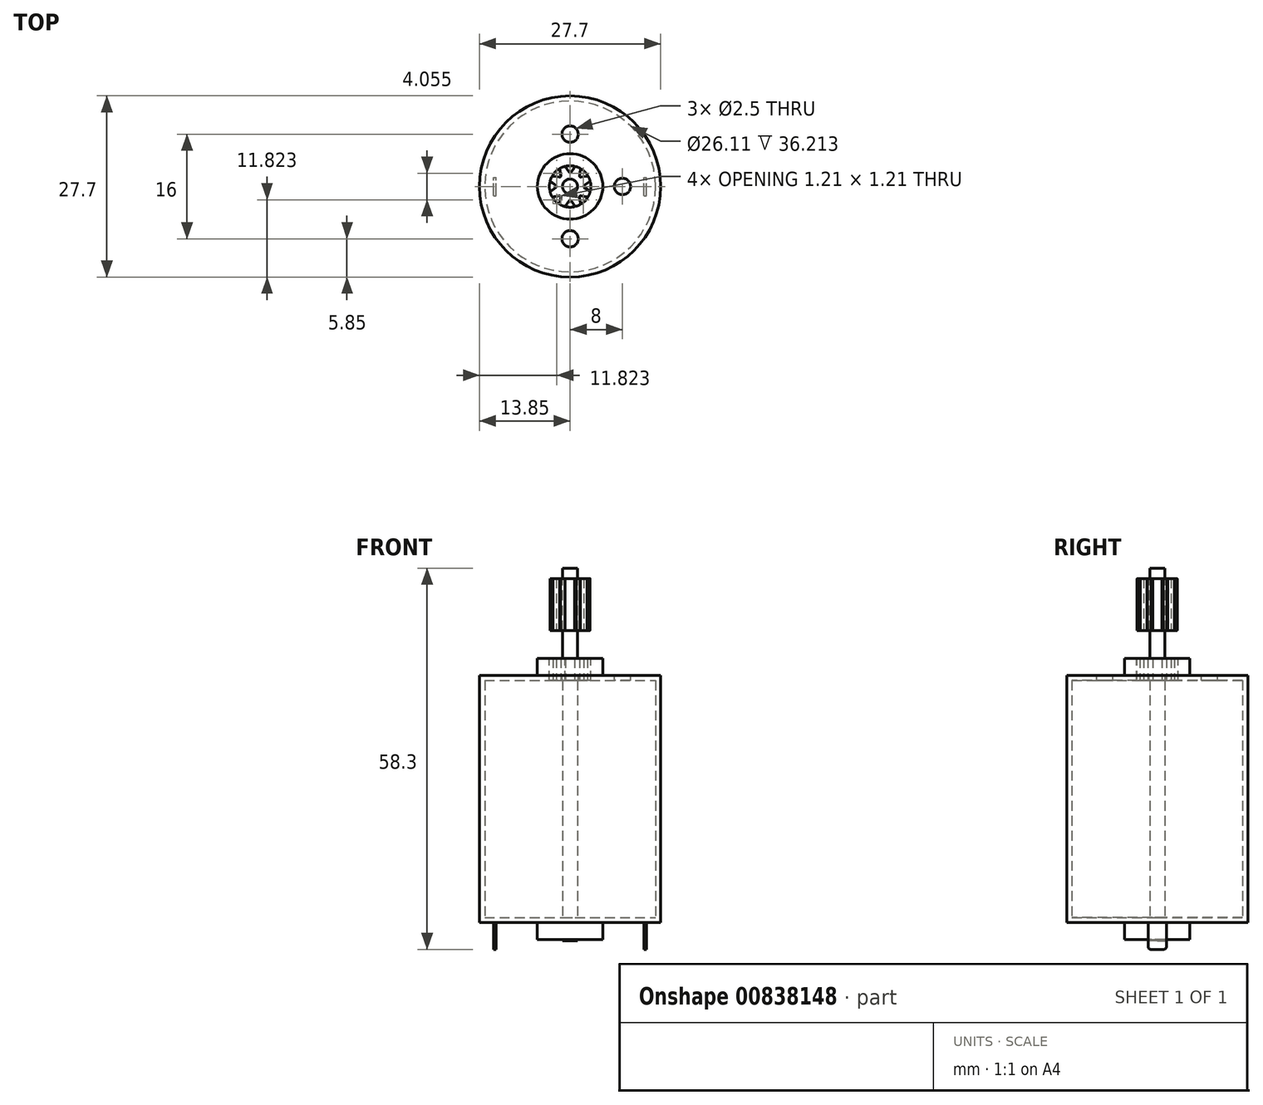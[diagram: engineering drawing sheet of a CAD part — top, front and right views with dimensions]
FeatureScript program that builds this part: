
annotation { "Feature Type Name" : "Feature", "Feature Type Description" : "" }
export const myFeature = defineFeature(function(context is Context, id is Id, definition is map)
    precondition{}
    {
        {
            var Q0;
            Q0=qCreatedBy(makeId("Top.planeOp"),FACE);
            var sketch = newSketch(context, id + "F0", { "sketchPlane" : qUnion([Q0])});
            skCircle(sketch, "E0", {"center": v(0, 0) * mm, "radius": 13.85 * mm});
            skSolve(sketch);
        }
        {
            var Q0;
            Q0=makeQuery(id+"F0.imprint","IMPRINT",FACE,{"disambiguationData":[TD([[makeQuery(id+"F0.imprint","IMPRINT",EDGE,{"derivedFrom":sQuery(id+"F0.wireOp",EDGE,"E0")}),1.0]])]});
            extrude(context, id + "F1", {"entities" : qUnion([Q0]), "depth" : 37.8 * mm, "offsetDistance" : 25.4 * mm});
        }
        {
            var Q0;
            Q0=makeQuery(id+"F1.opExtrude","CAP_FACE",FACE,{"disambiguationData":[OSD([sQuery(id+"F0.wireOp",EDGE,"E0")])],"isStart":false});
            var sketch = newSketch(context, id + "F2", { "sketchPlane" : qUnion([Q0])});
            skCircle(sketch, "E1", {"center": v(0, 0) * mm, "radius": 5 * mm});
            skSolve(sketch);
        }
        {
            var Q0;
            Q0=makeQuery(id+"F2.imprint","IMPRINT",FACE,{"disambiguationData":[TD([[makeQuery(id+"F2.imprint","IMPRINT",EDGE,{"derivedFrom":sQuery(id+"F2.wireOp",EDGE,"E1")}),1.0]])]});
            extrude(context, id + "F3", {"entities" : qUnion([Q0]), "operationType" : NewBodyOperationType.ADD, "depth" : 2.6 * mm, "offsetDistance" : 25.4 * mm});
        }
        {
            var Q0;
            Q0=makeQuery(id+"F1.opExtrude","CAP_FACE",FACE,{"disambiguationData":[OSD([sQuery(id+"F0.wireOp",EDGE,"E0")])],"isStart":false});
            var sketch = newSketch(context, id + "F4", { "sketchPlane" : qUnion([Q0])});
            skCircle(sketch, "E2", {"center": v(0, 8) * mm, "radius": 1.25 * mm});
            skCircle(sketch, "E3", {"center": v(0, -8) * mm, "radius": 1.25 * mm});
            skCircle(sketch, "E4", {"center": v(8, 0) * mm, "radius": 1.25 * mm});
            skSolve(sketch);
        }
        {
            var Q0;
            Q0=makeQuery(id+"F4.imprint","IMPRINT",FACE,{"disambiguationData":[TD([[makeQuery(id+"F4.imprint","IMPRINT",EDGE,{"derivedFrom":sQuery(id+"F4.wireOp",EDGE,"E2")}),1.0]])]});
            var Q1;
            Q1=makeQuery(id+"F4.imprint","IMPRINT",FACE,{"disambiguationData":[TD([[makeQuery(id+"F4.imprint","IMPRINT",EDGE,{"derivedFrom":sQuery(id+"F4.wireOp",EDGE,"E4")}),1.0]])]});
            var Q2;
            Q2=makeQuery(id+"F4.imprint","IMPRINT",FACE,{"disambiguationData":[TD([[makeQuery(id+"F4.imprint","IMPRINT",EDGE,{"derivedFrom":sQuery(id+"F4.wireOp",EDGE,"E3")}),1.0]])]});
            extrude(context, id + "F5", {"entities" : qUnion([Q0, Q1, Q2]), "operationType" : NewBodyOperationType.REMOVE, "oppositeDirection" : true, "depth" : 0.8 * mm, "offsetDistance" : 25.4 * mm});
        }
        {
            var Q0;
            Q0=makeQuery(id+"F1.opExtrude","CAP_FACE",FACE,{"disambiguationData":[OSD([sQuery(id+"F0.wireOp",EDGE,"E0")])],"isStart":true});
            var sketch = newSketch(context, id + "F6", { "sketchPlane" : qUnion([Q0])});
            skCircle(sketch, "E5", {"center": v(0, 0) * mm, "radius": 13.06 * mm});
            skSolve(sketch);
        }
        {
            var Q0;
            Q0=makeQuery(id+"F6.imprint","IMPRINT",FACE,{"disambiguationData":[TD([[makeQuery(id+"F6.imprint","IMPRINT",EDGE,{"derivedFrom":sQuery(id+"F6.wireOp",EDGE,"E5")}),1.0]])]});
            extrude(context, id + "F7", {"entities" : qUnion([Q0]), "operationType" : NewBodyOperationType.REMOVE, "oppositeDirection" : true, "depth" : 37 * mm, "offsetDistance" : 25.4 * mm});
        }
        {
            var Q0;
            Q0=makeQuery(id+"F3.opExtrude","CAP_FACE",FACE,{"disambiguationData":[OSD([sQuery(id+"F2.wireOp",EDGE,"E1")])],"isStart":false});
            var sketch = newSketch(context, id + "F8", { "sketchPlane" : qUnion([Q0])});
            skCircle(sketch, "E6", {"center": v(0, 0) * mm, "radius": 1.15 * mm});
            skSolve(sketch);
        }
        {
            var Q0;
            Q0=makeQuery(id+"F8.imprint","IMPRINT",FACE,{"disambiguationData":[TD([[makeQuery(id+"F8.imprint","IMPRINT",EDGE,{"derivedFrom":sQuery(id+"F8.wireOp",EDGE,"E6")}),1.0]])]});
            extrude(context, id + "F9", {"entities" : qUnion([Q0]), "operationType" : NewBodyOperationType.REMOVE, "oppositeDirection" : true, "depth" : 50.8 * mm, "offsetDistance" : 25.4 * mm});
        }
        {
            var Q0;
            Q0=makeQuery(id+"F3.opExtrude","CAP_FACE",FACE,{"disambiguationData":[OSD([sQuery(id+"F2.wireOp",EDGE,"E1")])],"isStart":false});
            var sketch = newSketch(context, id + "F10", { "sketchPlane" : qUnion([Q0])});
            skCircle(sketch, "E7", {"center": v(0, 0) * mm, "radius": 1.15 * mm});
            skSolve(sketch);
        }
        {
            var Q0;
            Q0=makeQuery(id+"F1.opExtrude","CAP_FACE",FACE,{"disambiguationData":[OSD([sQuery(id+"F0.wireOp",EDGE,"E0")])],"isStart":true});
            var sketch = newSketch(context, id + "F11", { "sketchPlane" : qUnion([Q0])});
            skCircle(sketch, "E8", {"center": v(0, 0) * mm, "radius": 13.06 * mm});
            skSolve(sketch);
        }
        {
            var Q0;
            Q0=makeQuery(id+"F11.imprint","IMPRINT",FACE,{"disambiguationData":[TD([[makeQuery(id+"F11.imprint","IMPRINT",EDGE,{"derivedFrom":sQuery(id+"F11.wireOp",EDGE,"E8")}),1.0]])]});
            extrude(context, id + "F12", {"entities" : qUnion([Q0]), "operationType" : NewBodyOperationType.ADD, "oppositeDirection" : true, "depth" : 0.8 * mm, "offsetDistance" : 25.4 * mm});
        }
        {
            var Q0;
            Q0=makeQuery(id+"F12.boolean.opBoolean","MERGE",FACE,{"derivedFrom":[makeQuery(id+"F1.opExtrude","CAP_FACE",FACE,{"disambiguationData":[OSD([sQuery(id+"F0.wireOp",EDGE,"E0")])],"isStart":true}),makeQuery(id+"F12.opExtrude","CAP_FACE",FACE,{"disambiguationData":[OSD([sQuery(id+"F11.wireOp",EDGE,"E8")])],"isStart":true})]});
            var sketch = newSketch(context, id + "F13", { "sketchPlane" : qUnion([Q0])});
            skCircle(sketch, "E9", {"center": v(0, 0) * mm, "radius": 5 * mm});
            skSolve(sketch);
        }
        {
            var Q0;
            Q0=makeQuery(id+"F13.imprint","IMPRINT",FACE,{"disambiguationData":[TD([[makeQuery(id+"F13.imprint","IMPRINT",EDGE,{"derivedFrom":sQuery(id+"F13.wireOp",EDGE,"E9")}),1.0]])]});
            extrude(context, id + "F14", {"entities" : qUnion([Q0]), "operationType" : NewBodyOperationType.ADD, "depth" : 2.6 * mm, "offsetDistance" : 25.4 * mm});
        }
        {
            var Q0;
            Q0=makeQuery(id+"F14.opExtrude","CAP_FACE",FACE,{"disambiguationData":[OSD([sQuery(id+"F13.wireOp",EDGE,"E9")])],"isStart":false});
            var sketch = newSketch(context, id + "F15", { "sketchPlane" : qUnion([Q0])});
            skCircle(sketch, "E10", {"center": v(0, 0) * mm, "radius": 1.15 * mm});
            skSolve(sketch);
        }
        {
            var Q0;
            Q0=makeQuery(id+"F15.imprint","IMPRINT",FACE,{"disambiguationData":[TD([[makeQuery(id+"F15.imprint","IMPRINT",EDGE,{"derivedFrom":sQuery(id+"F15.wireOp",EDGE,"E10")}),1.0]])]});
            extrude(context, id + "F16", {"entities" : qUnion([Q0]), "operationType" : NewBodyOperationType.REMOVE, "oppositeDirection" : true, "depth" : 25.4 * mm, "offsetDistance" : 25.4 * mm});
        }
        {
            var Q0;
            Q0=makeQuery(id+"F10.imprint","IMPRINT",FACE,{"disambiguationData":[TD([[makeQuery(id+"F10.imprint","IMPRINT",EDGE,{"derivedFrom":sQuery(id+"F10.wireOp",EDGE,"E7")}),1.0]])]});
            extrude(context, id + "F17", {"entities" : qUnion([Q0]), "depth" : 13.8 * mm, "offsetDistance" : 25.4 * mm});
        }
        {
            var Q0;
            Q0=makeQuery(id+"F17.opExtrude","CAP_FACE",FACE,{"disambiguationData":[OSD([sQuery(id+"F10.wireOp",EDGE,"E7")])],"isStart":true});
            extrude(context, id + "F18", {"entities" : qUnion([Q0]), "operationType" : NewBodyOperationType.ADD, "depth" : 43.2 * mm, "offsetDistance" : 25.4 * mm});
        }
        {
            var Q0;
            Q0=makeQuery(id+"F12.boolean.opBoolean","MERGE",FACE,{"derivedFrom":[makeQuery(id+"F1.opExtrude","CAP_FACE",FACE,{"disambiguationData":[OSD([sQuery(id+"F0.wireOp",EDGE,"E0")])],"isStart":true}),makeQuery(id+"F12.opExtrude","CAP_FACE",FACE,{"disambiguationData":[OSD([sQuery(id+"F11.wireOp",EDGE,"E8")])],"isStart":true})]});
            var sketch = newSketch(context, id + "F19", { "sketchPlane" : qUnion([Q0])});
            skLineSegment(sketch, "E11.bottom", {"start": v(-11.7, 1.4) * mm, "end": v(-11.3, 1.4) * mm});
            skLineSegment(sketch, "E11.top", {"start": v(-11.7, -1.4) * mm, "end": v(-11.3, -1.4) * mm});
            skLineSegment(sketch, "E11.left", {"start": v(-11.7, 1.4) * mm, "end": v(-11.7, -1.4) * mm});
            skLineSegment(sketch, "E11.right", {"start": v(-11.3, 1.4) * mm, "end": v(-11.3, -1.4) * mm});
            skLineSegment(sketch, "E12.bottom", {"start": v(11.3, 1.4) * mm, "end": v(11.7, 1.4) * mm});
            skLineSegment(sketch, "E12.top", {"start": v(11.3, -1.4) * mm, "end": v(11.7, -1.4) * mm});
            skLineSegment(sketch, "E12.left", {"start": v(11.3, 1.4) * mm, "end": v(11.3, -1.4) * mm});
            skLineSegment(sketch, "E12.right", {"start": v(11.7, 1.4) * mm, "end": v(11.7, -1.4) * mm});
            skPoint(sketch, "E13.endSnap0", {"position": v(11.3, 0) * mm});
            skSolve(sketch);
        }
        {
            var Q0;
            Q0=makeQuery(id+"F19.imprint","IMPRINT",FACE,{"disambiguationData":[TD([[makeQuery(id+"F19.imprint","IMPRINT",EDGE,{"derivedFrom":sQuery(id+"F19.wireOp",EDGE,"E11.bottom")}),-1.0]])]});
            var Q1;
            Q1=makeQuery(id+"F19.imprint","IMPRINT",FACE,{"disambiguationData":[TD([[makeQuery(id+"F19.imprint","IMPRINT",EDGE,{"derivedFrom":sQuery(id+"F19.wireOp",EDGE,"E12.bottom")}),-1.0]])]});
            extrude(context, id + "F20", {"entities" : qUnion([Q0, Q1]), "depth" : 4.1 * mm, "offsetDistance" : 25.4 * mm});
        }
        {
            var Q0;
            Q0=makeQuery(id+"F20.opExtrude","CAP_EDGE",EDGE,{"disambiguationData":[OSD([sQuery(id+"F19.wireOp",EDGE,"E12.bottom")])],"isStart":false});
            var Q1;
            Q1=makeQuery(id+"F20.opExtrude","CAP_EDGE",EDGE,{"disambiguationData":[OSD([sQuery(id+"F19.wireOp",EDGE,"E12.top")])],"isStart":false});
            var Q2;
            Q2=makeQuery(id+"F20.opExtrude","CAP_EDGE",EDGE,{"disambiguationData":[OSD([sQuery(id+"F19.wireOp",EDGE,"E11.top")])],"isStart":false});
            var Q3;
            Q3=makeQuery(id+"F20.opExtrude","CAP_EDGE",EDGE,{"disambiguationData":[OSD([sQuery(id+"F19.wireOp",EDGE,"E11.bottom")])],"isStart":false});
            fillet(context, id + "F21", {"entities" : qUnion([Q0, Q1, Q2, Q3]), "radius" : 0.4 * mm, "tangentPropagation" : true, "allowEdgeOverflow" : false});
        }
        {
            var Q0;
            Q0=makeQuery(id+"F17.opExtrude","CAP_FACE",FACE,{"disambiguationData":[OSD([sQuery(id+"F10.wireOp",EDGE,"E7")])],"isStart":false});
            var sketch = newSketch(context, id + "F22", { "sketchPlane" : qUnion([Q0])});
            skCircle(sketch, "E14", {"center": v(0, 0) * mm, "radius": 3.17 * mm});
            skSolve(sketch);
        }
        {
            var Q0;
            Q0=makeQuery(id+"F22.imprint","IMPRINT",FACE,{"disambiguationData":[TD([[makeQuery(id+"F22.imprint","IMPRINT",EDGE,{"derivedFrom":sQuery(id+"F22.wireOp",EDGE,"E14")}),1.0]])]});
            extrude(context, id + "F23", {"entities" : qUnion([Q0]), "oppositeDirection" : true, "depth" : 9.52 * mm, "offsetDistance" : 25.4 * mm});
        }
        {
            var Q0;
            Q0=makeQuery(id+"F23.opExtrude","CAP_FACE",FACE,{"disambiguationData":[OSD([sQuery(id+"F10.wireOp",EDGE,"E7"),sQuery(id+"F22.wireOp",EDGE,"E14")])],"isStart":true});
            extrude(context, id + "F24", {"entities" : qUnion([Q0]), "operationType" : NewBodyOperationType.REMOVE, "oppositeDirection" : true, "depth" : 1.59 * mm, "offsetDistance" : 25.4 * mm});
        }
        {
            var Q0;
            Q0=makeQuery(id+"F24.boolean.opBoolean","COPY",FACE,{"derivedFrom":makeQuery(id+"F24.opExtrude","CAP_FACE",FACE,{"disambiguationData":[OSD([sQuery(id+"F10.wireOp",EDGE,"E7"),sQuery(id+"F22.wireOp",EDGE,"E14")])],"isStart":false})});
            var sketch = newSketch(context, id + "F25", { "sketchPlane" : qUnion([Q0])});
            skLineSegment(sketch, "E15", {"start": v(-1.94, 0) * mm, "end": v(-3.07, 0.8) * mm});
            skLineSegment(sketch, "E16", {"start": v(-3.07, 0.8) * mm, "end": v(-3.87, 0) * mm});
            skLineSegment(sketch, "E17", {"start": v(-3.87, 0) * mm, "end": v(-3.07, -0.8) * mm});
            skLineSegment(sketch, "E18", {"start": v(-3.07, -0.8) * mm, "end": v(-1.94, 0) * mm});
            skLineSegment(sketch, "E19", {"start": v(1.94, 0) * mm, "end": v(3.07, 0.8) * mm});
            skLineSegment(sketch, "E20", {"start": v(3.07, 0.8) * mm, "end": v(3.95, 0) * mm});
            skLineSegment(sketch, "E21", {"start": v(3.95, 0) * mm, "end": v(3.07, -0.8) * mm});
            skLineSegment(sketch, "E22", {"start": v(3.07, -0.8) * mm, "end": v(1.94, 0) * mm});
            skLineSegment(sketch, "E23", {"start": v(0, 1.94) * mm, "end": v(-0.8, 3.07) * mm});
            skLineSegment(sketch, "E24", {"start": v(-0.8, 3.07) * mm, "end": v(0, 3.67) * mm});
            skLineSegment(sketch, "E25", {"start": v(0, 3.67) * mm, "end": v(0.8, 3.07) * mm});
            skLineSegment(sketch, "E26", {"start": v(0.8, 3.07) * mm, "end": v(0, 1.94) * mm});
            skLineSegment(sketch, "E27", {"start": v(0, -1.94) * mm, "end": v(-0.8, -3.07) * mm});
            skLineSegment(sketch, "E28", {"start": v(-0.8, -3.07) * mm, "end": v(0, -3.63) * mm});
            skLineSegment(sketch, "E29", {"start": v(0, -3.63) * mm, "end": v(0.8, -3.07) * mm});
            skLineSegment(sketch, "E30", {"start": v(0.8, -3.07) * mm, "end": v(0, -1.94) * mm});
            skLineSegment(sketch, "E31", {"start": v(-1.37, -1.37) * mm, "end": v(-2.74, -1.61) * mm});
            skLineSegment(sketch, "E32", {"start": v(-2.74, -1.61) * mm, "end": v(-2.74, -2.74) * mm});
            skLineSegment(sketch, "E33", {"start": v(-2.74, -2.74) * mm, "end": v(-1.61, -2.74) * mm});
            skLineSegment(sketch, "E34", {"start": v(-1.61, -2.74) * mm, "end": v(-1.37, -1.37) * mm});
            skLineSegment(sketch, "E35", {"start": v(1.37, -1.37) * mm, "end": v(1.61, -2.74) * mm});
            skLineSegment(sketch, "E36", {"start": v(1.61, -2.74) * mm, "end": v(3.24, -2.74) * mm});
            skLineSegment(sketch, "E37", {"start": v(3.24, -2.74) * mm, "end": v(2.74, -1.61) * mm});
            skLineSegment(sketch, "E38", {"start": v(2.74, -1.61) * mm, "end": v(1.37, -1.37) * mm});
            skLineSegment(sketch, "E39", {"start": v(-1.37, 1.37) * mm, "end": v(-2.74, 1.61) * mm});
            skLineSegment(sketch, "E40", {"start": v(-2.74, 1.61) * mm, "end": v(-3.02, 2.64) * mm});
            skLineSegment(sketch, "E41", {"start": v(-3.02, 2.64) * mm, "end": v(-1.61, 2.74) * mm});
            skLineSegment(sketch, "E42", {"start": v(-1.61, 2.74) * mm, "end": v(-1.37, 1.37) * mm});
            skLineSegment(sketch, "E43", {"start": v(1.61, 2.74) * mm, "end": v(1.37, 1.37) * mm});
            skLineSegment(sketch, "E44", {"start": v(1.37, 1.37) * mm, "end": v(2.74, 1.61) * mm});
            skLineSegment(sketch, "E45", {"start": v(2.74, 1.61) * mm, "end": v(3.29, 2.61) * mm});
            skLineSegment(sketch, "E46", {"start": v(3.29, 2.61) * mm, "end": v(1.61, 2.74) * mm});
            skSolve(sketch);
        }
        {
            var Q0;
            {var subQ0=sQuery(id+"F25.wireOp",EDGE,"E39");Q0=makeQuery(id+"F25.imprint","IMPRINT",FACE,{"disambiguationData":[TD([[makeQuery(id+"F25.imprint","IMPRINT",EDGE,{"derivedFrom":subQ0}),-1.0]])]});}
            var Q1;
            {var subQ0=sQuery(id+"F25.wireOp",EDGE,"E23");Q1=makeQuery(id+"F25.imprint","IMPRINT",FACE,{"disambiguationData":[TD([[makeQuery(id+"F25.imprint","IMPRINT",EDGE,{"derivedFrom":subQ0}),-1.0]])]});}
            var Q2;
            {var subQ0=sQuery(id+"F25.wireOp",EDGE,"E43");Q2=makeQuery(id+"F25.imprint","IMPRINT",FACE,{"disambiguationData":[TD([[makeQuery(id+"F25.imprint","IMPRINT",EDGE,{"derivedFrom":subQ0}),1.0]])]});}
            var Q3;
            {var subQ0=sQuery(id+"F25.wireOp",EDGE,"E19");Q3=makeQuery(id+"F25.imprint","IMPRINT",FACE,{"disambiguationData":[TD([[makeQuery(id+"F25.imprint","IMPRINT",EDGE,{"derivedFrom":subQ0}),-1.0]])]});}
            var Q4;
            {var subQ0=sQuery(id+"F25.wireOp",EDGE,"E35");Q4=makeQuery(id+"F25.imprint","IMPRINT",FACE,{"disambiguationData":[TD([[makeQuery(id+"F25.imprint","IMPRINT",EDGE,{"derivedFrom":subQ0}),1.0]])]});}
            var Q5;
            {var subQ0=sQuery(id+"F25.wireOp",EDGE,"E27");Q5=makeQuery(id+"F25.imprint","IMPRINT",FACE,{"disambiguationData":[TD([[makeQuery(id+"F25.imprint","IMPRINT",EDGE,{"derivedFrom":subQ0}),1.0]])]});}
            var Q6;
            {var subQ0=sQuery(id+"F25.wireOp",EDGE,"E31");Q6=makeQuery(id+"F25.imprint","IMPRINT",FACE,{"disambiguationData":[TD([[makeQuery(id+"F25.imprint","IMPRINT",EDGE,{"derivedFrom":subQ0}),1.0]])]});}
            var Q7;
            {var subQ0=sQuery(id+"F25.wireOp",EDGE,"E15");Q7=makeQuery(id+"F25.imprint","IMPRINT",FACE,{"disambiguationData":[TD([[makeQuery(id+"F25.imprint","IMPRINT",EDGE,{"derivedFrom":subQ0}),1.0]])]});}
            extrude(context, id + "F26", {"entities" : qUnion([Q0, Q1, Q2, Q3, Q4, Q5, Q6, Q7]), "operationType" : NewBodyOperationType.REMOVE, "oppositeDirection" : true, "depth" : 25.4 * mm, "offsetDistance" : 25.4 * mm});
        }
        {
            var Q0;
            Q0=makeQuery(id+"F26.boolean.opBoolean","COPY",EDGE,{"derivedFrom":makeQuery(id+"F26.opExtrude","SWEPT_EDGE",EDGE,{"disambiguationData":[OSD([sQuery(id+"F25.wireOp",EDGE,"E39"),sQuery(id+"F25.wireOp",EDGE,"E42")])]})});
            var Q1;
            Q1=makeQuery(id+"F26.boolean.opBoolean","COPY",EDGE,{"derivedFrom":makeQuery(id+"F26.opExtrude","SWEPT_EDGE",EDGE,{"disambiguationData":[OSD([sQuery(id+"F25.wireOp",EDGE,"E23"),sQuery(id+"F25.wireOp",EDGE,"E26")])]})});
            var Q2;
            Q2=makeQuery(id+"F26.boolean.opBoolean","COPY",EDGE,{"derivedFrom":makeQuery(id+"F26.opExtrude","SWEPT_EDGE",EDGE,{"disambiguationData":[OSD([sQuery(id+"F25.wireOp",EDGE,"E43"),sQuery(id+"F25.wireOp",EDGE,"E44")])]})});
            var Q3;
            Q3=makeQuery(id+"F26.boolean.opBoolean","COPY",EDGE,{"derivedFrom":makeQuery(id+"F26.opExtrude","SWEPT_EDGE",EDGE,{"disambiguationData":[OSD([sQuery(id+"F25.wireOp",EDGE,"E19"),sQuery(id+"F25.wireOp",EDGE,"E22")])]})});
            var Q4;
            Q4=makeQuery(id+"F26.boolean.opBoolean","COPY",EDGE,{"derivedFrom":makeQuery(id+"F26.opExtrude","SWEPT_EDGE",EDGE,{"disambiguationData":[OSD([sQuery(id+"F25.wireOp",EDGE,"E35"),sQuery(id+"F25.wireOp",EDGE,"E38")])]})});
            var Q5;
            Q5=makeQuery(id+"F26.boolean.opBoolean","COPY",EDGE,{"derivedFrom":makeQuery(id+"F26.opExtrude","SWEPT_EDGE",EDGE,{"disambiguationData":[OSD([sQuery(id+"F25.wireOp",EDGE,"E27"),sQuery(id+"F25.wireOp",EDGE,"E30")])]})});
            var Q6;
            Q6=makeQuery(id+"F26.boolean.opBoolean","COPY",EDGE,{"derivedFrom":makeQuery(id+"F26.opExtrude","SWEPT_EDGE",EDGE,{"disambiguationData":[OSD([sQuery(id+"F25.wireOp",EDGE,"E31"),sQuery(id+"F25.wireOp",EDGE,"E34")])]})});
            var Q7;
            Q7=makeQuery(id+"F26.boolean.opBoolean","COPY",EDGE,{"derivedFrom":makeQuery(id+"F26.opExtrude","SWEPT_EDGE",EDGE,{"disambiguationData":[OSD([sQuery(id+"F25.wireOp",EDGE,"E15"),sQuery(id+"F25.wireOp",EDGE,"E18")])]})});
            fillet(context, id + "F27", {"entities" : qUnion([Q0, Q1, Q2, Q3, Q4, Q5, Q6, Q7]), "radius" : 0.2 * mm, "tangentPropagation" : true, "allowEdgeOverflow" : false});
        }
        {
            var Q0;
            Q0=makeQuery(id+"F26.boolean.opBoolean","COPY",EDGE,{"derivedFrom":makeQuery(id+"F26.opExtrude","SWEPT_EDGE",EDGE,{"disambiguationData":[OSD([sQuery(id+"F22.wireOp",EDGE,"E14"),sQuery(id+"F25.wireOp",EDGE,"E15"),sQuery(id+"F25.wireOp",EDGE,"E16")])]})});
            var Q1;
            Q1=makeQuery(id+"F26.boolean.opBoolean","COPY",EDGE,{"derivedFrom":makeQuery(id+"F26.opExtrude","SWEPT_EDGE",EDGE,{"disambiguationData":[OSD([sQuery(id+"F22.wireOp",EDGE,"E14"),sQuery(id+"F25.wireOp",EDGE,"E17"),sQuery(id+"F25.wireOp",EDGE,"E18")])]})});
            var Q2;
            Q2=makeQuery(id+"F26.boolean.opBoolean","COPY",EDGE,{"derivedFrom":makeQuery(id+"F26.opExtrude","SWEPT_EDGE",EDGE,{"disambiguationData":[OSD([sQuery(id+"F22.wireOp",EDGE,"E14"),sQuery(id+"F25.wireOp",EDGE,"E31"),sQuery(id+"F25.wireOp",EDGE,"E32")])]})});
            var Q3;
            Q3=makeQuery(id+"F26.boolean.opBoolean","COPY",EDGE,{"derivedFrom":makeQuery(id+"F26.opExtrude","SWEPT_EDGE",EDGE,{"disambiguationData":[OSD([sQuery(id+"F22.wireOp",EDGE,"E14"),sQuery(id+"F25.wireOp",EDGE,"E39"),sQuery(id+"F25.wireOp",EDGE,"E40")])]})});
            var Q4;
            Q4=makeQuery(id+"F26.boolean.opBoolean","COPY",EDGE,{"derivedFrom":makeQuery(id+"F26.opExtrude","SWEPT_EDGE",EDGE,{"disambiguationData":[OSD([sQuery(id+"F22.wireOp",EDGE,"E14"),sQuery(id+"F25.wireOp",EDGE,"E41"),sQuery(id+"F25.wireOp",EDGE,"E42")])]})});
            var Q5;
            Q5=makeQuery(id+"F26.boolean.opBoolean","COPY",EDGE,{"derivedFrom":makeQuery(id+"F26.opExtrude","SWEPT_EDGE",EDGE,{"disambiguationData":[OSD([sQuery(id+"F22.wireOp",EDGE,"E14"),sQuery(id+"F25.wireOp",EDGE,"E23"),sQuery(id+"F25.wireOp",EDGE,"E24")])]})});
            var Q6;
            Q6=makeQuery(id+"F26.boolean.opBoolean","COPY",EDGE,{"derivedFrom":makeQuery(id+"F26.opExtrude","SWEPT_EDGE",EDGE,{"disambiguationData":[OSD([sQuery(id+"F22.wireOp",EDGE,"E14"),sQuery(id+"F25.wireOp",EDGE,"E25"),sQuery(id+"F25.wireOp",EDGE,"E26")])]})});
            var Q7;
            Q7=makeQuery(id+"F26.boolean.opBoolean","COPY",EDGE,{"derivedFrom":makeQuery(id+"F26.opExtrude","SWEPT_EDGE",EDGE,{"disambiguationData":[OSD([sQuery(id+"F22.wireOp",EDGE,"E14"),sQuery(id+"F25.wireOp",EDGE,"E43"),sQuery(id+"F25.wireOp",EDGE,"E46")])]})});
            var Q8;
            Q8=makeQuery(id+"F26.boolean.opBoolean","COPY",EDGE,{"derivedFrom":makeQuery(id+"F26.opExtrude","SWEPT_EDGE",EDGE,{"disambiguationData":[OSD([sQuery(id+"F22.wireOp",EDGE,"E14"),sQuery(id+"F25.wireOp",EDGE,"E44"),sQuery(id+"F25.wireOp",EDGE,"E45")])]})});
            var Q9;
            Q9=makeQuery(id+"F26.boolean.opBoolean","COPY",EDGE,{"derivedFrom":makeQuery(id+"F26.opExtrude","SWEPT_EDGE",EDGE,{"disambiguationData":[OSD([sQuery(id+"F22.wireOp",EDGE,"E14"),sQuery(id+"F25.wireOp",EDGE,"E19"),sQuery(id+"F25.wireOp",EDGE,"E20")])]})});
            var Q10;
            Q10=makeQuery(id+"F26.boolean.opBoolean","COPY",EDGE,{"derivedFrom":makeQuery(id+"F26.opExtrude","SWEPT_EDGE",EDGE,{"disambiguationData":[OSD([sQuery(id+"F22.wireOp",EDGE,"E14"),sQuery(id+"F25.wireOp",EDGE,"E21"),sQuery(id+"F25.wireOp",EDGE,"E22")])]})});
            var Q11;
            Q11=makeQuery(id+"F26.boolean.opBoolean","COPY",EDGE,{"derivedFrom":makeQuery(id+"F26.opExtrude","SWEPT_EDGE",EDGE,{"disambiguationData":[OSD([sQuery(id+"F22.wireOp",EDGE,"E14"),sQuery(id+"F25.wireOp",EDGE,"E37"),sQuery(id+"F25.wireOp",EDGE,"E38")])]})});
            var Q12;
            Q12=makeQuery(id+"F26.boolean.opBoolean","COPY",EDGE,{"derivedFrom":makeQuery(id+"F26.opExtrude","SWEPT_EDGE",EDGE,{"disambiguationData":[OSD([sQuery(id+"F22.wireOp",EDGE,"E14"),sQuery(id+"F25.wireOp",EDGE,"E35"),sQuery(id+"F25.wireOp",EDGE,"E36")])]})});
            var Q13;
            Q13=makeQuery(id+"F26.boolean.opBoolean","COPY",EDGE,{"derivedFrom":makeQuery(id+"F26.opExtrude","SWEPT_EDGE",EDGE,{"disambiguationData":[OSD([sQuery(id+"F22.wireOp",EDGE,"E14"),sQuery(id+"F25.wireOp",EDGE,"E29"),sQuery(id+"F25.wireOp",EDGE,"E30")])]})});
            var Q14;
            Q14=makeQuery(id+"F26.boolean.opBoolean","COPY",EDGE,{"derivedFrom":makeQuery(id+"F26.opExtrude","SWEPT_EDGE",EDGE,{"disambiguationData":[OSD([sQuery(id+"F22.wireOp",EDGE,"E14"),sQuery(id+"F25.wireOp",EDGE,"E33"),sQuery(id+"F25.wireOp",EDGE,"E34")])]})});
            fillet(context, id + "F28", {"entities" : qUnion([Q0, Q1, Q2, Q3, Q4, Q5, Q6, Q7, Q8, Q9, Q10, Q11, Q12, Q13, Q14]), "radius" : 0.2 * mm, "tangentPropagation" : true, "rho" : 0.5, "crossSection" : FilletCrossSection.CONIC, "allowEdgeOverflow" : false});
        }
    });
